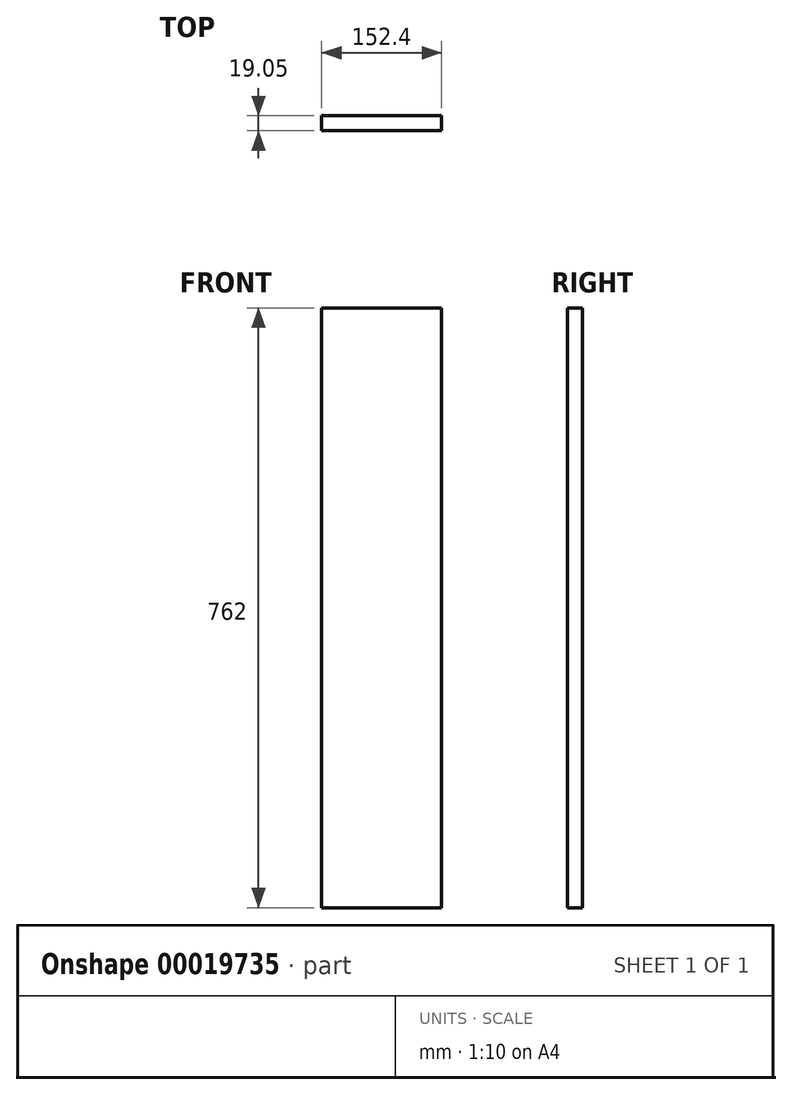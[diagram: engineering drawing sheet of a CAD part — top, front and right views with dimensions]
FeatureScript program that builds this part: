
annotation { "Feature Type Name" : "Feature", "Feature Type Description" : "" }
export const myFeature = defineFeature(function(context is Context, id is Id, definition is map)
    precondition{}
    {
        {
            var Q0;
            Q0=qCreatedBy(makeId("Top.planeOp"),FACE);
            var sketch = newSketch(context, id + "F0", { "sketchPlane" : qUnion([Q0])});
            skLineSegment(sketch, "E0.bottom", {"start": v(0, 0) * mm, "end": v(152.4, 0) * mm});
            skLineSegment(sketch, "E0.top", {"start": v(0, 19.05) * mm, "end": v(152.4, 19.05) * mm});
            skLineSegment(sketch, "E0.left", {"start": v(0, 0) * mm, "end": v(0, 19.05) * mm});
            skLineSegment(sketch, "E0.right", {"start": v(152.4, 0) * mm, "end": v(152.4, 19.05) * mm});
            skSolve(sketch);
        }
        {
            var Q0;
            Q0=makeQuery(id+"F0.imprint","IMPRINT",FACE,{"disambiguationData":[TD([[makeQuery(id+"F0.imprint","IMPRINT",EDGE,{"derivedFrom":sQuery(id+"F0.wireOp",EDGE,"E0.bottom")}),1.0]])]});
            extrude(context, id + "F1", {"entities" : qUnion([Q0]), "depth" : 762 * mm});
        }
    });
